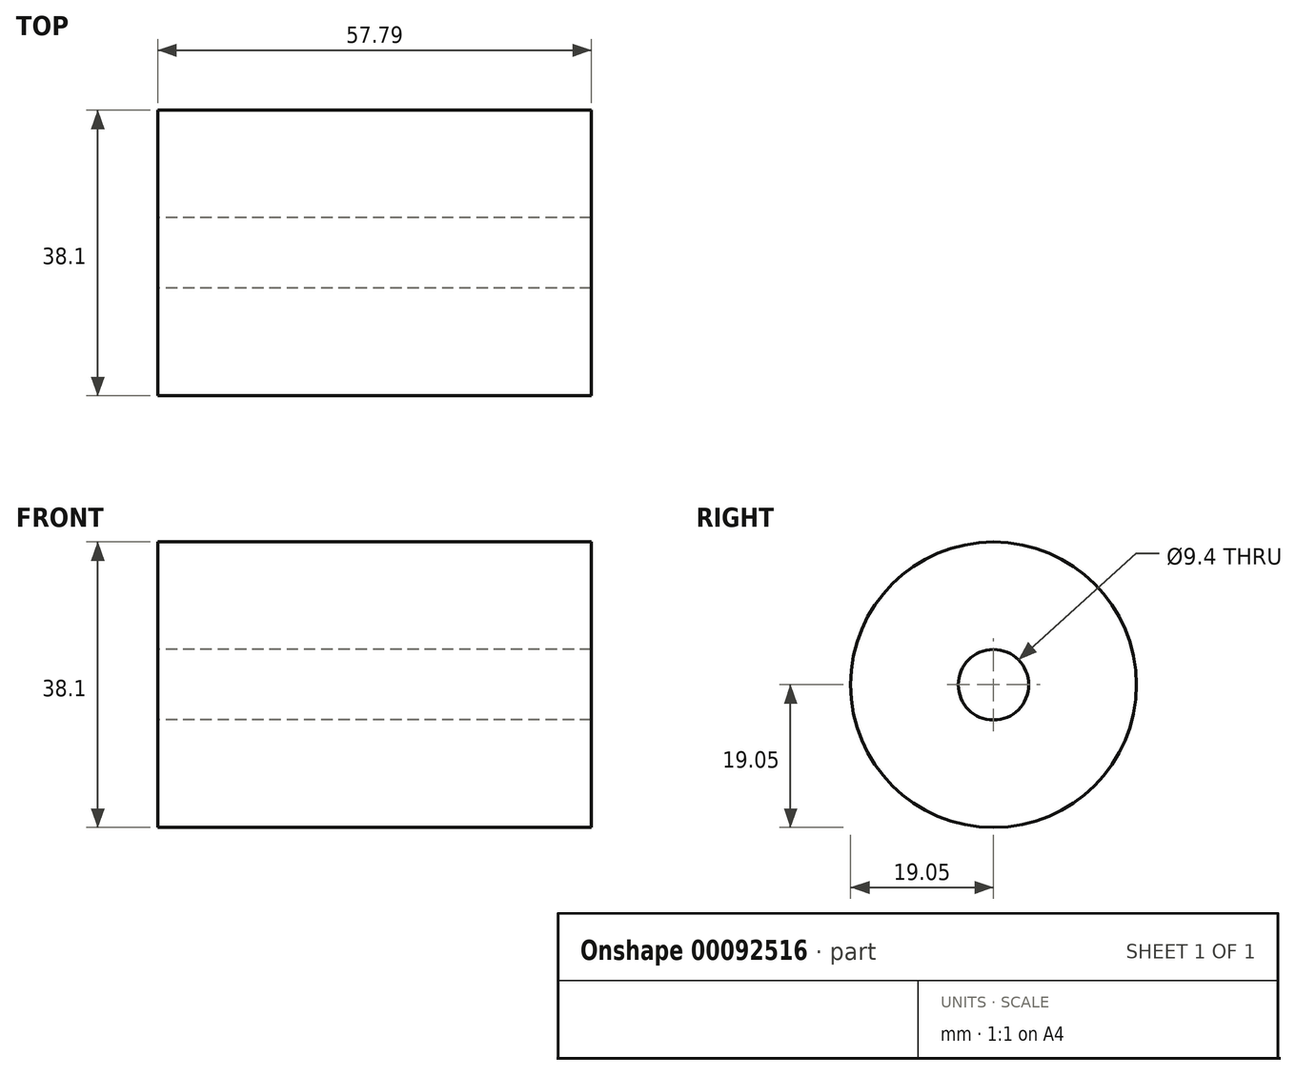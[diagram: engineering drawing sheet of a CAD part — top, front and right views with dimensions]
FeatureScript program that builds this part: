
annotation { "Feature Type Name" : "Feature", "Feature Type Description" : "" }
export const myFeature = defineFeature(function(context is Context, id is Id, definition is map)
    precondition{}
    {
        {
            var Q0;
            Q0=qCreatedBy(makeId("Right.planeOp"),FACE);
            var sketch = newSketch(context, id + "F0", { "sketchPlane" : qUnion([Q0])});
            skCircle(sketch, "E0", {"center": v(0, 0) * mm, "radius": 19.05 * mm});
            skCircle(sketch, "E1", {"center": v(0, 0) * mm, "radius": 4.7 * mm});
            skSolve(sketch);
        }
        {
            var Q0;
            Q0=makeQuery(id+"F0.imprint","IMPRINT",FACE,{"disambiguationData":[TD([[makeQuery(id+"F0.imprint","IMPRINT",EDGE,{"derivedFrom":sQuery(id+"F0.wireOp",EDGE,"E0")}),1.0]])]});
            extrude(context, id + "F1", {"entities" : qUnion([Q0]), "depth" : 57.78 * mm});
        }
    });
